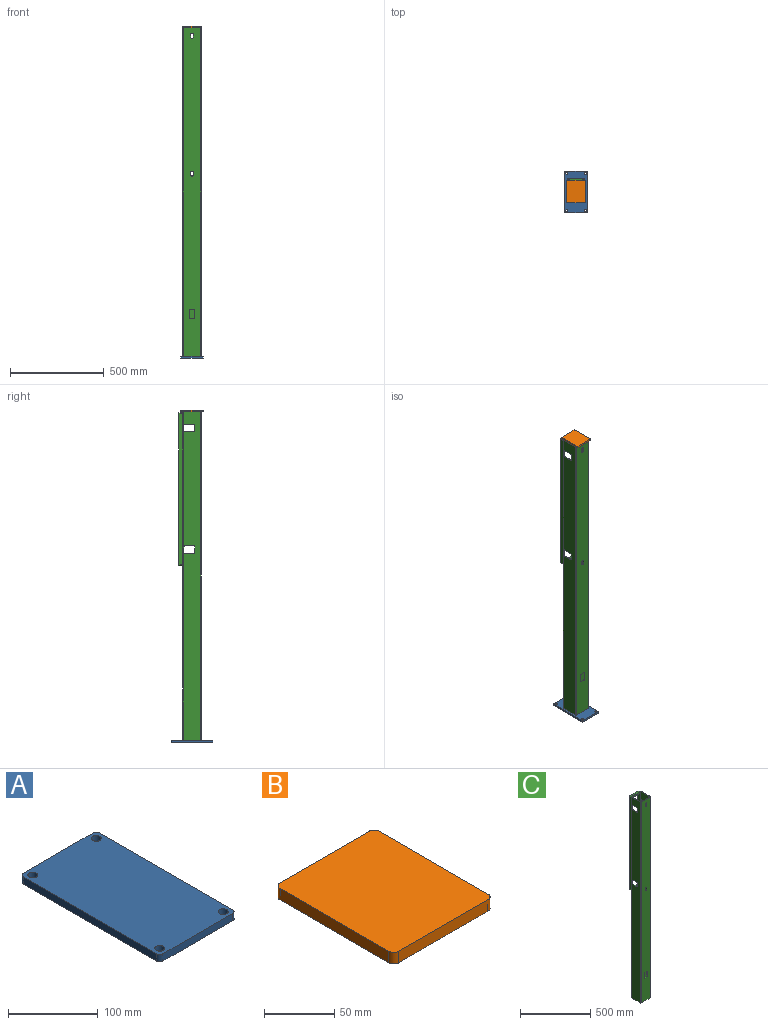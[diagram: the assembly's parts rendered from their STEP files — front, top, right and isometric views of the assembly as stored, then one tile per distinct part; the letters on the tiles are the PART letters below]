
ASSEMBLY  parts=3 mates=2
PART A: 14 faces, bbox 120x220x10 mm
  f0: plane 110x10mm, normal (0,-1,0), area 1100mm2, adj f1,f11,f12,f13
  f1: cylinder r=5mm len=10mm, axis (0,0,-1), area 78.5mm2, adj f0,f2,f12,f13
  f2: plane 210x10mm, normal (1,0,0), area 2100mm2, adj f1,f3,f12,f13
  f3: cylinder r=5mm len=10mm, axis (0,0,-1), area 78.5mm2, adj f2,f4,f12,f13
  f4: plane 110x10mm, normal (0,1,0), area 1100mm2, adj f3,f5,f12,f13
  f5: cylinder r=5mm len=10mm, axis (0,0,-1), area 78.5mm2, adj f4,f6,f12,f13
  f6: plane 210x10mm, normal (-1,0,0), area 2100mm2, adj f5,f11,f12,f13
  f7: cylinder r=5.5mm len=11mm, axis (0,0,-1), area 345.6mm2, adj f12,f13
  f8: cylinder r=5.5mm len=11mm, axis (0,0,-1), area 345.6mm2, adj f12,f13
  f9: cylinder r=5.5mm len=11mm, axis (0,0,-1), area 345.6mm2, adj f12,f13
  f10: cylinder r=5.5mm len=11mm, axis (0,0,-1), area 345.6mm2, adj f12,f13
  f11: cylinder r=5mm len=10mm, axis (0,0,-1), area 78.5mm2, adj f0,f6,f12,f13
  f12: plane 220x120mm, normal (0,0,1), area 25998.4mm2, adj f0,f1,f2,f3,f4,f5,f6,f7
  f13: plane 220x120mm, normal (0,0,-1), area 25998.4mm2, adj f0,f1,f2,f3,f4,f5,f6,f7
PART B: 10 faces, bbox 100x120x10 mm
  f0: plane 90x10mm, normal (0,-1,0), area 900mm2, adj f1,f7,f8,f9
  f1: cylinder r=5mm len=10mm, axis (0,0,-1), area 78.5mm2, adj f0,f2,f8,f9
  f2: plane 110x10mm, normal (1,0,0), area 1100mm2, adj f1,f3,f8,f9
  f3: cylinder r=5mm len=10mm, axis (0,0,-1), area 78.5mm2, adj f2,f4,f8,f9
  f4: plane 90x10mm, normal (0,1,0), area 900mm2, adj f3,f5,f8,f9
  f5: cylinder r=5mm len=10mm, axis (0,0,-1), area 78.5mm2, adj f4,f6,f8,f9
  f6: plane 110x10mm, normal (-1,0,0), area 1100mm2, adj f5,f7,f8,f9
  f7: cylinder r=5mm len=10mm, axis (0,0,-1), area 78.5mm2, adj f0,f6,f8,f9
  f8: plane 120x100mm, normal (0,0,1), area 11978.5mm2, adj f0,f1,f2,f3,f4,f5,f6,f7
  f9: plane 120x100mm, normal (0,0,-1), area 11978.5mm2, adj f0,f1,f2,f3,f4,f5,f6,f7
PART C: 83 faces, bbox 100x120x1750.5 mm
  f0: plane 4.85x3.78mm, normal (0,1,0), area 4.7mm2, adj f34,f35,f79
  f1: plane 90x10.15mm, normal (0,1,0), area 474.3mm2, adj f12,f14,f17,f73,f74,f75
  f2: plane 5x5mm, normal (0,1,0), area 5.4mm2, adj f28,f29,f35
  f3: plane 4.85x3.78mm, normal (0,1,0), area 4.7mm2, adj f31,f32,f80
  f4: plane 5x5mm, normal (0,1,0), area 5.4mm2, adj f29,f30,f31
  f5: plane 1750.5x90mm, normal (-1,0,0), area 152787.9mm2, adj f14,f15,f17,f18,f58,f59,f60,f61
  f6: plane 1750.5x90mm, normal (0,-1,0), area 155366.6mm2, adj f10,f15,f17,f18,f19,f20,f21,f22
  f7: plane 1750.5x90mm, normal (0,1,0), area 156845.1mm2, adj f8,f9,f17,f18,f36,f37,f38,f39
  f8: plane 1750.5x90mm, normal (-1,0,0), area 152787.9mm2, adj f7,f16,f17,f18,f44,f45,f46,f47
  f9: plane 1750.5x90mm, normal (1,0,0), area 152787.9mm2, adj f7,f16,f17,f18,f58,f59,f60,f61
  f10: cylinder r=5mm len=1750.5mm, axis (0,0,-1), area 13748.4mm2, adj f6,f11,f17,f18
  f11: plane 1750.5x90mm, normal (1,0,0), area 152787.9mm2, adj f10,f12,f17,f18,f44,f45,f46,f47
  f12: cylinder r=5mm len=1750.5mm, axis (0,0,-1), area 13748.4mm2, adj f1,f11,f13,f16,f17,f18,f76
  f13: plane 935.5x90mm, normal (0,1,0), area 83755.7mm2, adj f12,f14,f18,f77,f78,f81
  f14: cylinder r=5mm len=1750.5mm, axis (0,0,-1), area 13748.4mm2, adj f1,f5,f13,f16,f17,f18,f72
  f15: cylinder r=5mm len=1750.5mm, axis (0,0,-1), area 13748.4mm2, adj f5,f6,f17,f18
  f16: plane 1750.5x100mm, normal (0,-1,0), area 93766.5mm2, adj f8,f9,f12,f14,f17,f18,f28,f29
  f17: plane 100x100mm, normal (0,0,1), area 1878.5mm2, adj f1,f5,f6,f7,f8,f9,f10,f11
  f18: plane 100x100mm, normal (0,0,-1), area 1878.5mm2, adj f5,f6,f7,f8,f9,f10,f11,f12
  f19: plane 20x4mm, normal (0,0,-1), area 80mm2, adj f6,f20,f26,f27
  f20: cylinder r=5mm len=5mm, axis (0,-1,0), area 31.4mm2, adj f6,f19,f21,f27
  f21: plane 40x4mm, normal (1,0,0), area 160mm2, adj f6,f20,f22,f27
  f22: cylinder r=5mm len=5mm, axis (0,-1,0), area 31.4mm2, adj f6,f21,f23,f27
  f23: plane 20x4mm, normal (0,0,1), area 80mm2, adj f6,f22,f24,f27
  f24: cylinder r=5mm len=5mm, axis (0,-1,0), area 31.4mm2, adj f6,f23,f25,f27
  f25: plane 40x4mm, normal (-1,0,0), area 160mm2, adj f6,f24,f26,f27
  f26: cylinder r=5mm len=5mm, axis (0,-1,0), area 31.4mm2, adj f6,f19,f25,f27
  f27: plane 50x30mm, normal (0,-1,0), area 1478.5mm2, adj f19,f20,f21,f22,f23,f24,f25,f26
  f28: cylinder r=5mm len=5mm, axis (0,1,0), area 39.3mm2, adj f2,f16,f29,f35
  f29: plane 80x25mm, normal (0,0,1), area 1950mm2, adj f2,f4,f16,f28,f30,f31,f35,f82
  f30: cylinder r=5mm len=5mm, axis (0,1,0), area 39.3mm2, adj f4,f16,f29,f31
  f31: plane 804.85x25mm, normal (1,0,0), area 20072mm2, adj f3,f4,f16,f29,f30,f32,f80,f82
  f32: cylinder r=5mm len=25mm, axis (0,1,0), area 63.9mm2, adj f3,f16,f31,f33,f80,f82
  f33: plane 70x25mm, normal (0,0,-1), area 1750mm2, adj f16,f32,f34,f82
  f34: cylinder r=5mm len=25mm, axis (0,1,0), area 63.9mm2, adj f0,f16,f33,f35,f79,f82
  f35: plane 804.85x25mm, normal (-1,0,0), area 20072mm2, adj f0,f2,f16,f28,f29,f34,f79,f82
  f36: plane 14x5mm, normal (-1,0,0), area 70mm2, adj f6,f7,f37,f39
  f37: cylinder r=7mm len=14mm, axis (0,-1,0), area 110mm2, adj f6,f7,f36,f38
  f38: plane 14x5mm, normal (1,0,0), area 70mm2, adj f6,f7,f37,f39
  f39: cylinder r=7mm len=14mm, axis (0,-1,0), area 110mm2, adj f6,f7,f36,f38
  f40: plane 14x5mm, normal (1,0,0), area 70mm2, adj f6,f7,f41,f43
  f41: cylinder r=7mm len=14mm, axis (0,-1,0), area 110mm2, adj f6,f7,f40,f42
  f42: plane 14x5mm, normal (-1,0,0), area 70mm2, adj f6,f7,f41,f43
  f43: cylinder r=7mm len=14mm, axis (0,-1,0), area 110mm2, adj f6,f7,f40,f42
  f44: plane 50x5mm, normal (0,0,1), area 250mm2, adj f8,f11,f48,f49
  f45: plane 50x5mm, normal (0,0,-1), area 250mm2, adj f8,f11,f46,f50
  f46: cylinder r=5mm len=5mm, axis (1,0,0), area 39.3mm2, adj f8,f11,f45,f47
  f47: plane 30x5mm, normal (0,1,0), area 150mm2, adj f8,f11,f46,f48
  f48: cylinder r=5mm len=5mm, axis (1,0,0), area 39.3mm2, adj f8,f11,f44,f47
  f49: cylinder r=5mm len=5mm, axis (1,0,0), area 39.3mm2, adj f8,f11,f16,f44
  f50: cylinder r=5mm len=5mm, axis (1,0,0), area 39.3mm2, adj f8,f11,f16,f45
  f51: plane 50x5mm, normal (0,0,-1), area 250mm2, adj f8,f11,f52,f56
  f52: cylinder r=5mm len=5mm, axis (1,0,0), area 39.3mm2, adj f8,f11,f51,f53
  f53: plane 30x5mm, normal (0,1,0), area 150mm2, adj f8,f11,f52,f54
  f54: cylinder r=5mm len=5mm, axis (1,0,0), area 39.3mm2, adj f8,f11,f53,f55
  f55: plane 50x5mm, normal (0,0,1), area 250mm2, adj f8,f11,f54,f57
  f56: cylinder r=5mm len=5mm, axis (1,0,0), area 39.3mm2, adj f8,f11,f16,f51
  f57: cylinder r=5mm len=5mm, axis (1,0,0), area 39.3mm2, adj f8,f11,f16,f55
  f58: cylinder r=5mm len=5mm, axis (-1,0,0), area 39.3mm2, adj f5,f9,f16,f59
  f59: plane 50x5mm, normal (0,0,1), area 250mm2, adj f5,f9,f58,f60
  f60: cylinder r=5mm len=5mm, axis (-1,0,0), area 39.3mm2, adj f5,f9,f59,f61
  f61: plane 30x5mm, normal (0,1,0), area 150mm2, adj f5,f9,f60,f62
  f62: cylinder r=5mm len=5mm, axis (-1,0,0), area 39.3mm2, adj f5,f9,f61,f63
  f63: plane 50x5mm, normal (0,0,-1), area 250mm2, adj f5,f9,f62,f64
  f64: cylinder r=5mm len=5mm, axis (-1,0,0), area 39.3mm2, adj f5,f9,f16,f63
  f65: cylinder r=5mm len=5mm, axis (-1,0,0), area 39.3mm2, adj f5,f9,f16,f66
  f66: plane 50x5mm, normal (0,0,1), area 250mm2, adj f5,f9,f65,f67
  f67: cylinder r=5mm len=5mm, axis (-1,0,0), area 39.3mm2, adj f5,f9,f66,f68
  f68: plane 30x5mm, normal (0,1,0), area 150mm2, adj f5,f9,f67,f69
  f69: cylinder r=5mm len=5mm, axis (-1,0,0), area 39.3mm2, adj f5,f9,f68,f70
  f70: plane 50x5mm, normal (0,0,-1), area 250mm2, adj f5,f9,f69,f71
  f71: cylinder r=5mm len=5mm, axis (-1,0,0), area 39.3mm2, adj f5,f9,f16,f70
  f72: plane 804.85x20mm, normal (-1,0,0), area 16097mm2, adj f14,f73,f81,f82
  f73: cylinder r=5mm len=20mm, axis (0,-1,0), area 157.1mm2, adj f1,f72,f74,f82
  f74: plane 80x20mm, normal (0,0,1), area 1600mm2, adj f1,f73,f75,f82
  f75: cylinder r=5mm len=20mm, axis (0,-1,0), area 157.1mm2, adj f1,f74,f76,f82
  f76: plane 804.85x20mm, normal (1,0,0), area 16097mm2, adj f12,f75,f77,f82
  f77: cylinder r=5mm len=20mm, axis (0,-1,0), area 157.1mm2, adj f13,f76,f78,f82
  f78: plane 80x20mm, normal (0,0,-1), area 1600mm2, adj f13,f77,f81,f82
  f79: plane 20x3.78mm, normal (0,0,-1), area 75.7mm2, adj f0,f34,f35,f82
  f80: plane 20x3.78mm, normal (0,0,-1), area 75.7mm2, adj f3,f31,f32,f82
  f81: cylinder r=5mm len=20mm, axis (0,-1,0), area 157.1mm2, adj f13,f72,f78,f82
  f82: plane 814.85x90mm, normal (0,1,0), area 8916.3mm2, adj f29,f31,f32,f33,f34,f35,f72,f73
PLACE A t=(-127.76,-16.7,266.43)mm
PLACE B t=(-127.76,-16.7,2026.93)mm
PLACE C t=(-127.76,-16.7,276.43)mm
MATE planar A.f12 <-> C.f18  axis (0,0,1) through (-127.76,-16.7,276.43)mm
MATE planar B.f9 <-> C.f17  axis (0,0,-1) through (-177.76,-16.7,2026.93)mm
